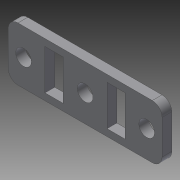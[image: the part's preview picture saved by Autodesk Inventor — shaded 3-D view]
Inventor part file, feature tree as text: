
AUTODESK INVENTOR PART (.ipt)
format: ipt  version: 2015 (Build 190159000, 159)  size: 106,496 bytes
history: native  units: in
note: dims shown in document units (in); Inventor stores cm internally (conversion verified against a paired STEP export)
features: extrude x1, sketch x1
ambient origin geometry x8: Origin, YZ Plane, XZ Plane, XY Plane, X Axis, Y Axis, Z Axis, Center Point
bodies: Solid1 (feature_tree)
feature tree (2):
  extrude  "Extrusion1"  Depth=1.378in
  sketch  "Sketch1"  dims[d0=3.937in d1=1.378in d2=3.1496in d3=0.4016in d4=0.25in d5=0.0in d6=0.4016in d7=0.25in d8=1.0273in d9=0.4665in]
